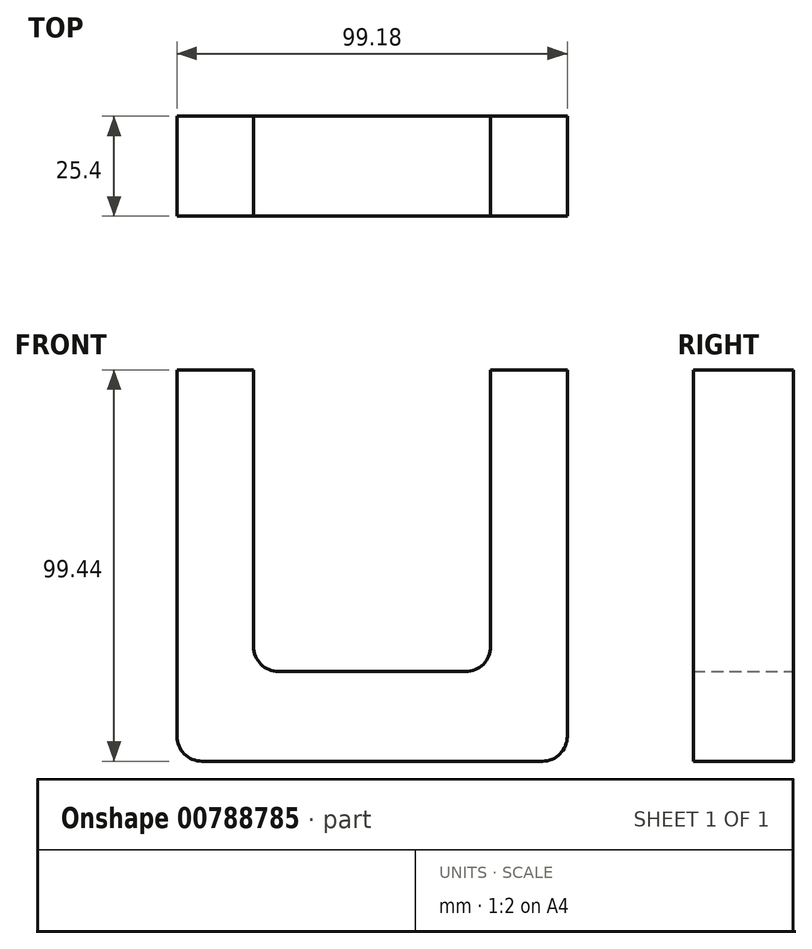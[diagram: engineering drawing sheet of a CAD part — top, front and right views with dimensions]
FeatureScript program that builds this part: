
annotation { "Feature Type Name" : "Feature", "Feature Type Description" : "" }
export const myFeature = defineFeature(function(context is Context, id is Id, definition is map)
    precondition{}
    {
        {
            var Q0;
            Q0=qCreatedBy(makeId("Front.planeOp"),FACE);
            var sketch = newSketch(context, id + "F0", { "sketchPlane" : qUnion([Q0])});
            skLineSegment(sketch, "E0", {"start": v(-99.18, 57.79) * mm, "end": v(-99.18, -35.3) * mm});
            skLineSegment(sketch, "E1", {"start": v(-92.83, -41.65) * mm, "end": v(-6.35, -41.65) * mm});
            skLineSegment(sketch, "E2", {"start": v(0, -35.3) * mm, "end": v(0, 57.79) * mm});
            skLineSegment(sketch, "E3", {"start": v(-99.18, 57.79) * mm, "end": v(-79.7, 57.79) * mm});
            skLineSegment(sketch, "E4", {"start": v(-79.7, 57.79) * mm, "end": v(-79.7, -12.53) * mm});
            skLineSegment(sketch, "E5", {"start": v(-73.35, -18.88) * mm, "end": v(-25.83, -18.88) * mm});
            skLineSegment(sketch, "E6", {"start": v(-19.48, -12.53) * mm, "end": v(-19.48, 57.79) * mm});
            skLineSegment(sketch, "E7", {"start": v(-19.48, 57.79) * mm, "end": v(0, 57.79) * mm});
            skPoint(sketch, "E8.visualSharp", {"position": v(-79.7, -18.88) * mm});
            skArc(sketch, "E8.filletArc", {"start": v(-79.7, -12.53) * mm, "mid": v(-77.84, -17.02) * mm, "end": v(-73.35, -18.88) * mm});
            skPoint(sketch, "E9.visualSharp", {"position": v(-19.48, -18.88) * mm});
            skArc(sketch, "E9.filletArc", {"start": v(-25.83, -18.88) * mm, "mid": v(-21.34, -17.02) * mm, "end": v(-19.48, -12.53) * mm});
            skPoint(sketch, "E10.visualSharp", {"position": v(0, -41.65) * mm});
            skArc(sketch, "E10.filletArc", {"start": v(-6.35, -41.65) * mm, "mid": v(-1.86, -39.79) * mm, "end": v(0, -35.3) * mm});
            skPoint(sketch, "E11.visualSharp", {"position": v(-99.18, -41.65) * mm});
            skArc(sketch, "E11.filletArc", {"start": v(-99.18, -35.3) * mm, "mid": v(-97.32, -39.79) * mm, "end": v(-92.83, -41.65) * mm});
            skSolve(sketch);
        }
        {
            var Q0;
            Q0=makeQuery(id+"F0.imprint","IMPRINT",FACE,{"disambiguationData":[TD([[makeQuery(id+"F0.imprint","IMPRINT",EDGE,{"derivedFrom":sQuery(id+"F0.wireOp",EDGE,"E0")}),1.0]])]});
            extrude(context, id + "F1", {"entities" : qUnion([Q0]), "depth" : 25.4 * mm, "offsetDistance" : 25.4 * mm});
        }
    });
